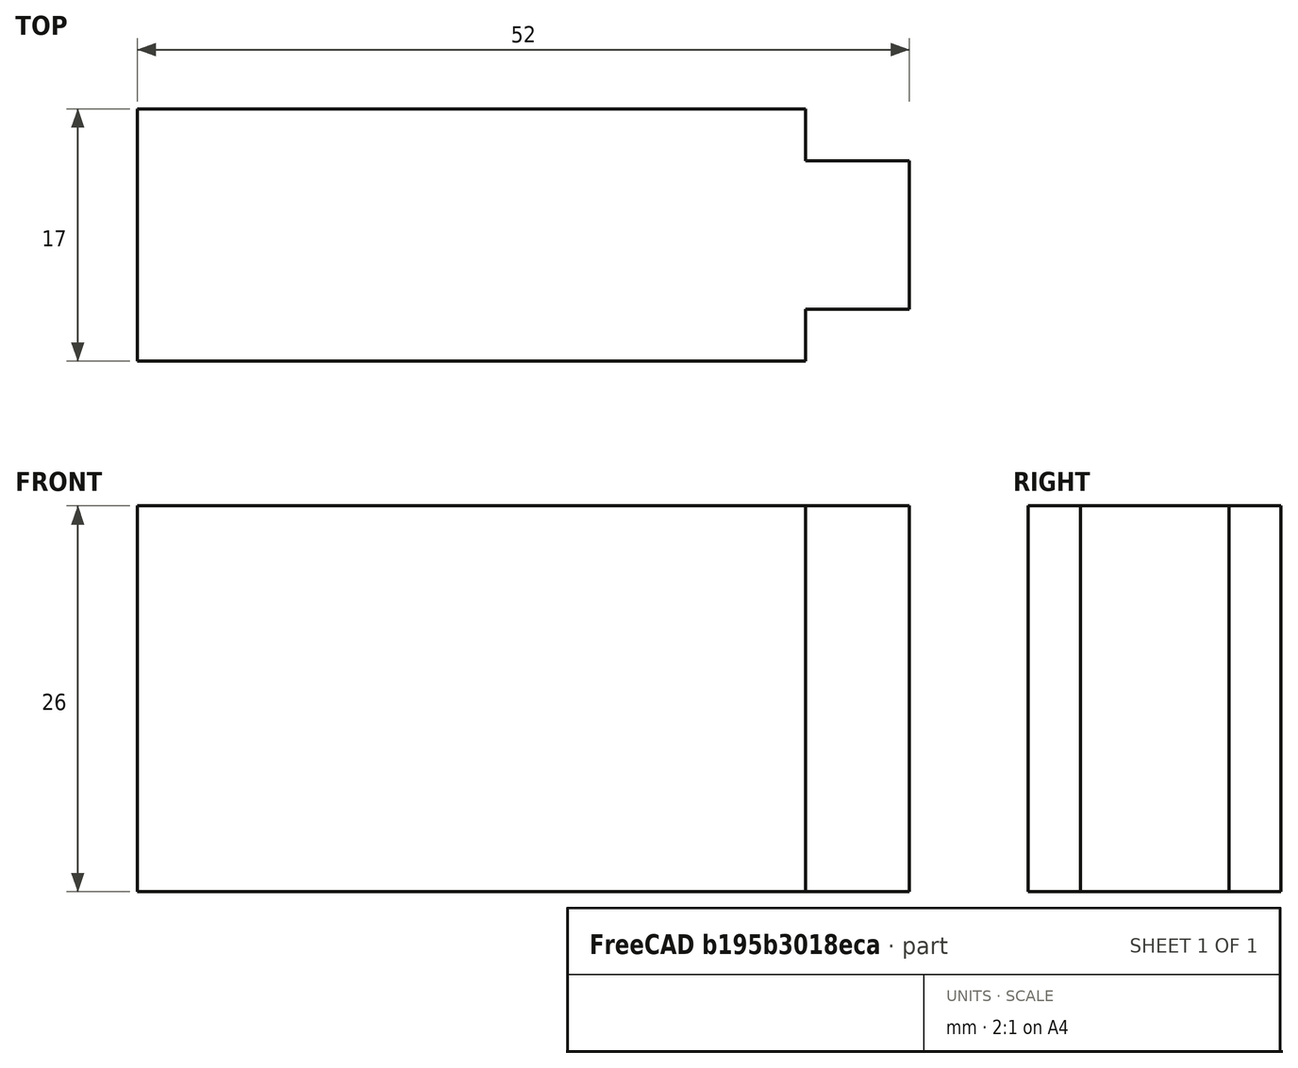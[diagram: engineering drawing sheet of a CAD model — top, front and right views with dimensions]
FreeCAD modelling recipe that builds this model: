
FCSTD DOCUMENT  (FreeCAD 0.14R3700 (Git))
Label: BIRR_pile9V
License: CC-BY 3.0
LicenseURL: http://creativecommons.org/licenses/by/3.0/
objects: Sketcher::SketchObject×1, Part::Extrusion×1, Part::Feature×1
note: 3 computed .brp shape members not serialized (recipe doc carries the construction recipe); baked Part::Feature solids carry a one-line shape summary decoded from their .brp

FEATURE [Sketcher::SketchObject] Sketch  label="pile9V"
  sketch-geometry (8):
    g0: LineSegment StartX=-26 StartY=8.5 StartZ=0 EndX=19 EndY=8.5 EndZ=0
    g1: LineSegment StartX=19 StartY=-8.5 StartZ=0 EndX=-26 EndY=-8.5 EndZ=0
    g2: LineSegment StartX=-26 StartY=-8.5 StartZ=0 EndX=-26 EndY=8.5 EndZ=0
    g3: LineSegment StartX=19 StartY=8.5 StartZ=0 EndX=19 EndY=5 EndZ=0
    g4: LineSegment StartX=19 StartY=5 StartZ=0 EndX=26 EndY=5 EndZ=0
    g5: LineSegment StartX=26 StartY=5 StartZ=0 EndX=26 EndY=-5 EndZ=0
    g6: LineSegment StartX=26 StartY=-5 StartZ=0 EndX=19 EndY=-5 EndZ=0
    g7: LineSegment StartX=19 StartY=-5 StartZ=0 EndX=19 EndY=-8.5 EndZ=0
  constraints (23):
    c: Coincident(g1,g2)
    c: Coincident(g2,g0)
    c: Horizontal(g0)
    c: Horizontal(g1)
    c: Vertical(g2)
    c: Symmetric(g0,g1,g-1)
    c: DistanceX(g0) = 45
    c: DistanceY(g2) = 17
    c: Vertical(g3)
    c: Coincident(g4,g3)
    c: Vertical(g5)
    c: Coincident(g6,g5)
    c: Coincident(g7,g6)
    c: Coincident(g7,g1)
    c: Vertical(g7)
    c: Horizontal(g6)
    c: DistanceX(g-1,g0) = -26
    c: Coincident(g3,g0)
    c: Symmetric(g3,g6,g-1)
    c: Horizontal(g4)
    c: DistanceX(g5,g1) = -52
    c: Coincident(g4,g5)
    c: DistanceY(g5) = -10
FEATURE [Part::Extrusion] Extrude
  Base = -> Sketch
  Dir = (0,0,26)
  Solid = true
FEATURE [Part::Feature] Extrude001  label="pile9V_copy"
  shape: bbox 52 x 17 x 26 mm, 10 faces (baked)
